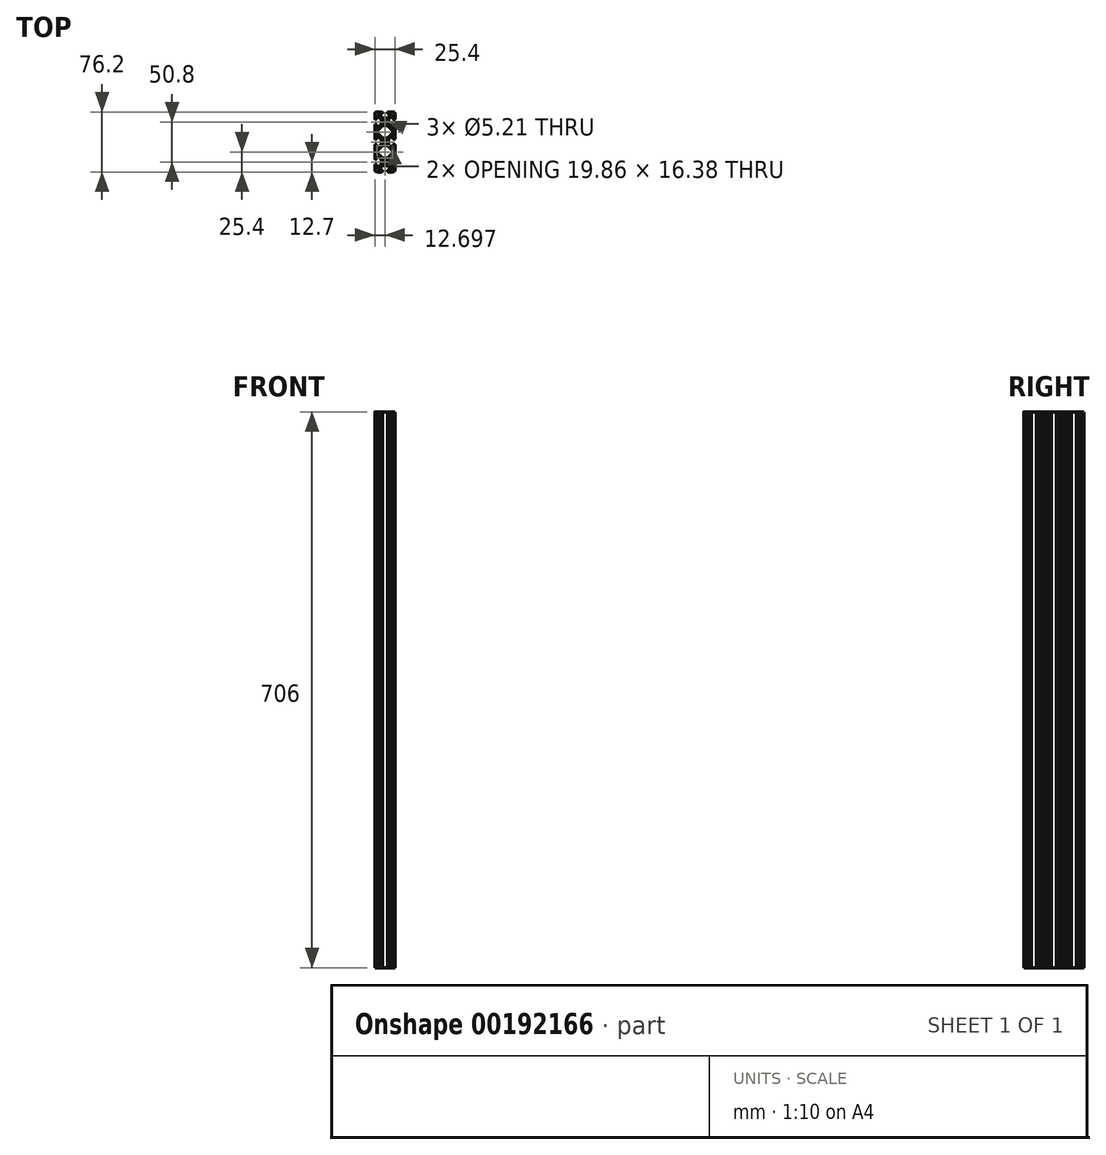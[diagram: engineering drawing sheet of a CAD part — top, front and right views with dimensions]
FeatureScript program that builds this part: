
annotation { "Feature Type Name" : "Feature", "Feature Type Description" : "" }
export const myFeature = defineFeature(function(context is Context, id is Id, definition is map)
    precondition{}
    {
        {
            var Q0;
            Q0=qCreatedBy(makeId("Top.planeOp"),FACE);
            var sketch = newSketch(context, id + "F0", { "sketchPlane" : qUnion([Q0])});
            skArc(sketch, "E0.0.0", {"start": v(-125.85, 41.51) * mm, "mid": v(-126.36, 41) * mm, "end": v(-126.87, 41.51) * mm});
            skArc(sketch, "E0.0.1", {"start": v(-126.87, 41.51) * mm, "mid": v(-128.39, 40.9) * mm, "end": v(-129, 39.38) * mm});
            skArc(sketch, "E0.0.2", {"start": v(-129, 39.38) * mm, "mid": v(-128.5, 38.87) * mm, "end": v(-129, 38.36) * mm});
            skLineSegment(sketch, "E0.0.3", {"start": v(-129, 38.36) * mm, "end": v(-129, 35.13) * mm});
            skArc(sketch, "E0.0.4", {"start": v(-129, 35.13) * mm, "mid": v(-128.5, 34.63) * mm, "end": v(-129, 34.12) * mm});
            skLineSegment(sketch, "E0.0.5", {"start": v(-129, 34.12) * mm, "end": v(-129, 33.11) * mm});
            skArc(sketch, "E0.0.6", {"start": v(-129, 33.11) * mm, "mid": v(-127.9, 32) * mm, "end": v(-126.8, 33.11) * mm});
            skLineSegment(sketch, "E0.0.7", {"start": v(-126.8, 33.11) * mm, "end": v(-126.8, 35.28) * mm});
            skArc(sketch, "E0.0.8", {"start": v(-126.8, 35.28) * mm, "mid": v(-126.17, 36.22) * mm, "end": v(-125.06, 36) * mm});
            skLineSegment(sketch, "E0.0.9", {"start": v(-125.06, 36) * mm, "end": v(-121.74, 32.69) * mm});
            skArc(sketch, "E0.0.10", {"start": v(-121.74, 32.69) * mm, "mid": v(-121.05, 31.66) * mm, "end": v(-120.81, 30.44) * mm});
            skLineSegment(sketch, "E0.0.11", {"start": v(-120.81, 30.44) * mm, "end": v(-120.81, 27.18) * mm});
            skArc(sketch, "E0.0.12", {"start": v(-120.81, 27.18) * mm, "mid": v(-121.05, 25.96) * mm, "end": v(-121.74, 24.93) * mm});
            skLineSegment(sketch, "E0.0.13", {"start": v(-121.74, 24.93) * mm, "end": v(-125.06, 21.62) * mm});
            skArc(sketch, "E0.0.14", {"start": v(-125.06, 21.62) * mm, "mid": v(-126.17, 21.4) * mm, "end": v(-126.8, 22.34) * mm});
            skLineSegment(sketch, "E0.0.15", {"start": v(-126.8, 22.34) * mm, "end": v(-126.8, 24.5) * mm});
            skArc(sketch, "E0.0.16", {"start": v(-126.8, 24.5) * mm, "mid": v(-127.9, 25.61) * mm, "end": v(-129, 24.5) * mm});
            skLineSegment(sketch, "E0.0.17", {"start": v(-129, 24.5) * mm, "end": v(-129, 23.5) * mm});
            skArc(sketch, "E0.0.18", {"start": v(-129, 23.5) * mm, "mid": v(-128.5, 23) * mm, "end": v(-129, 22.49) * mm});
            skLineSegment(sketch, "E0.0.19", {"start": v(-129, 22.49) * mm, "end": v(-129, 19.26) * mm});
            skArc(sketch, "E0.0.20", {"start": v(-129, 19.26) * mm, "mid": v(-128.5, 18.75) * mm, "end": v(-129, 18.24) * mm});
            skLineSegment(sketch, "E0.0.21", {"start": v(-129, 18.24) * mm, "end": v(-129, 13.98) * mm});
            skArc(sketch, "E0.0.22", {"start": v(-129, 13.98) * mm, "mid": v(-128.5, 13.47) * mm, "end": v(-129, 12.96) * mm});
            skLineSegment(sketch, "E0.0.23", {"start": v(-129, 12.96) * mm, "end": v(-129, 9.73) * mm});
            skArc(sketch, "E0.0.24", {"start": v(-129, 9.73) * mm, "mid": v(-128.5, 9.23) * mm, "end": v(-129, 8.72) * mm});
            skLineSegment(sketch, "E0.0.25", {"start": v(-129, 8.72) * mm, "end": v(-129, 7.71) * mm});
            skArc(sketch, "E0.0.26", {"start": v(-129, 7.71) * mm, "mid": v(-127.9, 6.6) * mm, "end": v(-126.8, 7.71) * mm});
            skLineSegment(sketch, "E0.0.27", {"start": v(-126.8, 7.71) * mm, "end": v(-126.8, 9.88) * mm});
            skArc(sketch, "E0.0.28", {"start": v(-126.8, 9.88) * mm, "mid": v(-126.17, 10.82) * mm, "end": v(-125.06, 10.6) * mm});
            skLineSegment(sketch, "E0.0.29", {"start": v(-125.06, 10.6) * mm, "end": v(-121.74, 7.29) * mm});
            skArc(sketch, "E0.0.30", {"start": v(-121.74, 7.29) * mm, "mid": v(-121.05, 6.26) * mm, "end": v(-120.81, 5.04) * mm});
            skLineSegment(sketch, "E0.0.31", {"start": v(-120.81, 5.04) * mm, "end": v(-120.81, 1.78) * mm});
            skArc(sketch, "E0.0.32", {"start": v(-120.81, 1.78) * mm, "mid": v(-121.05, 0.56) * mm, "end": v(-121.74, -0.47) * mm});
            skLineSegment(sketch, "E0.0.33", {"start": v(-121.74, -0.47) * mm, "end": v(-125.06, -3.78) * mm});
            skArc(sketch, "E0.0.34", {"start": v(-125.06, -3.78) * mm, "mid": v(-126.17, -4) * mm, "end": v(-126.8, -3.06) * mm});
            skLineSegment(sketch, "E0.0.35", {"start": v(-126.8, -3.06) * mm, "end": v(-126.8, -0.9) * mm});
            skArc(sketch, "E0.0.36", {"start": v(-126.8, -0.9) * mm, "mid": v(-127.9, 0.21) * mm, "end": v(-129, -0.9) * mm});
            skLineSegment(sketch, "E0.0.37", {"start": v(-129, -0.9) * mm, "end": v(-129, -1.9) * mm});
            skArc(sketch, "E0.0.38", {"start": v(-129, -1.9) * mm, "mid": v(-128.5, -2.4) * mm, "end": v(-129, -2.91) * mm});
            skLineSegment(sketch, "E0.0.39", {"start": v(-129, -2.91) * mm, "end": v(-129, -6.14) * mm});
            skArc(sketch, "E0.0.40", {"start": v(-129, -6.14) * mm, "mid": v(-128.5, -6.65) * mm, "end": v(-129, -7.16) * mm});
            skLineSegment(sketch, "E0.0.41", {"start": v(-129, -7.16) * mm, "end": v(-129, -11.42) * mm});
            skArc(sketch, "E0.0.42", {"start": v(-129, -11.42) * mm, "mid": v(-128.5, -11.93) * mm, "end": v(-129, -12.44) * mm});
            skLineSegment(sketch, "E0.0.43", {"start": v(-129, -12.44) * mm, "end": v(-129, -15.67) * mm});
            skArc(sketch, "E0.0.44", {"start": v(-129, -15.67) * mm, "mid": v(-128.5, -16.17) * mm, "end": v(-129, -16.68) * mm});
            skLineSegment(sketch, "E0.0.45", {"start": v(-129, -16.68) * mm, "end": v(-129, -17.69) * mm});
            skArc(sketch, "E0.0.46", {"start": v(-129, -17.69) * mm, "mid": v(-127.9, -18.8) * mm, "end": v(-126.8, -17.69) * mm});
            skLineSegment(sketch, "E0.0.47", {"start": v(-126.8, -17.69) * mm, "end": v(-126.8, -15.52) * mm});
            skArc(sketch, "E0.0.48", {"start": v(-126.8, -15.52) * mm, "mid": v(-126.17, -14.58) * mm, "end": v(-125.06, -14.8) * mm});
            skLineSegment(sketch, "E0.0.49", {"start": v(-125.06, -14.8) * mm, "end": v(-121.74, -18.11) * mm});
            skArc(sketch, "E0.0.50", {"start": v(-121.74, -18.11) * mm, "mid": v(-121.05, -19.14) * mm, "end": v(-120.81, -20.36) * mm});
            skLineSegment(sketch, "E0.0.51", {"start": v(-120.81, -20.36) * mm, "end": v(-120.81, -23.62) * mm});
            skArc(sketch, "E0.0.52", {"start": v(-120.81, -23.62) * mm, "mid": v(-121.05, -24.84) * mm, "end": v(-121.74, -25.87) * mm});
            skLineSegment(sketch, "E0.0.53", {"start": v(-121.74, -25.87) * mm, "end": v(-125.06, -29.18) * mm});
            skArc(sketch, "E0.0.54", {"start": v(-125.06, -29.18) * mm, "mid": v(-126.17, -29.4) * mm, "end": v(-126.8, -28.46) * mm});
            skLineSegment(sketch, "E0.0.55", {"start": v(-126.8, -28.46) * mm, "end": v(-126.8, -26.3) * mm});
            skArc(sketch, "E0.0.56", {"start": v(-126.8, -26.3) * mm, "mid": v(-127.9, -25.19) * mm, "end": v(-129, -26.3) * mm});
            skLineSegment(sketch, "E0.0.57", {"start": v(-129, -26.3) * mm, "end": v(-129, -27.3) * mm});
            skArc(sketch, "E0.0.58", {"start": v(-129, -27.3) * mm, "mid": v(-128.5, -27.8) * mm, "end": v(-129, -28.31) * mm});
            skLineSegment(sketch, "E0.0.59", {"start": v(-129, -28.31) * mm, "end": v(-129, -31.54) * mm});
            skArc(sketch, "E0.0.60", {"start": v(-129, -31.54) * mm, "mid": v(-128.5, -32.05) * mm, "end": v(-129, -32.56) * mm});
            skArc(sketch, "E0.0.61", {"start": v(-129, -32.56) * mm, "mid": v(-128.39, -34.07) * mm, "end": v(-126.87, -34.69) * mm});
            skArc(sketch, "E0.0.62", {"start": v(-126.87, -34.69) * mm, "mid": v(-126.36, -34.18) * mm, "end": v(-125.85, -34.69) * mm});
            skLineSegment(sketch, "E0.0.63", {"start": v(-125.85, -34.69) * mm, "end": v(-122.63, -34.69) * mm});
            skArc(sketch, "E0.0.64", {"start": v(-122.63, -34.69) * mm, "mid": v(-122.12, -34.18) * mm, "end": v(-121.61, -34.69) * mm});
            skLineSegment(sketch, "E0.0.65", {"start": v(-121.61, -34.69) * mm, "end": v(-120.6, -34.69) * mm});
            skArc(sketch, "E0.0.66", {"start": v(-120.6, -34.69) * mm, "mid": v(-119.5, -33.59) * mm, "end": v(-120.6, -32.48) * mm});
            skLineSegment(sketch, "E0.0.67", {"start": v(-120.6, -32.48) * mm, "end": v(-122.78, -32.48) * mm});
            skArc(sketch, "E0.0.68", {"start": v(-122.78, -32.48) * mm, "mid": v(-123.72, -31.85) * mm, "end": v(-123.5, -30.75) * mm});
            skLineSegment(sketch, "E0.0.69", {"start": v(-123.5, -30.75) * mm, "end": v(-120.18, -27.43) * mm});
            skArc(sketch, "E0.0.70", {"start": v(-120.18, -27.43) * mm, "mid": v(-119.15, -26.74) * mm, "end": v(-117.93, -26.5) * mm});
            skLineSegment(sketch, "E0.0.71", {"start": v(-117.93, -26.5) * mm, "end": v(-114.67, -26.5) * mm});
            skArc(sketch, "E0.0.72", {"start": v(-114.67, -26.5) * mm, "mid": v(-113.46, -26.74) * mm, "end": v(-112.43, -27.43) * mm});
            skLineSegment(sketch, "E0.0.73", {"start": v(-112.43, -27.43) * mm, "end": v(-109.11, -30.75) * mm});
            skArc(sketch, "E0.0.74", {"start": v(-109.11, -30.75) * mm, "mid": v(-108.89, -31.85) * mm, "end": v(-109.83, -32.48) * mm});
            skLineSegment(sketch, "E0.0.75", {"start": v(-109.83, -32.48) * mm, "end": v(-112, -32.48) * mm});
            skArc(sketch, "E0.0.76", {"start": v(-112, -32.48) * mm, "mid": v(-113.1, -33.59) * mm, "end": v(-112, -34.69) * mm});
            skLineSegment(sketch, "E0.0.77", {"start": v(-112, -34.69) * mm, "end": v(-111, -34.69) * mm});
            skArc(sketch, "E0.0.78", {"start": v(-111, -34.69) * mm, "mid": v(-110.49, -34.18) * mm, "end": v(-109.98, -34.69) * mm});
            skLineSegment(sketch, "E0.0.79", {"start": v(-109.98, -34.69) * mm, "end": v(-106.75, -34.69) * mm});
            skArc(sketch, "E0.0.80", {"start": v(-106.75, -34.69) * mm, "mid": v(-106.24, -34.18) * mm, "end": v(-105.74, -34.69) * mm});
            skArc(sketch, "E0.0.81", {"start": v(-105.74, -34.69) * mm, "mid": v(-104.22, -34.07) * mm, "end": v(-103.6, -32.56) * mm});
            skArc(sketch, "E0.0.82", {"start": v(-103.6, -32.56) * mm, "mid": v(-104.11, -32.05) * mm, "end": v(-103.6, -31.54) * mm});
            skLineSegment(sketch, "E0.0.83", {"start": v(-103.6, -31.54) * mm, "end": v(-103.6, -28.31) * mm});
            skArc(sketch, "E0.0.84", {"start": v(-103.6, -28.31) * mm, "mid": v(-104.11, -27.8) * mm, "end": v(-103.6, -27.3) * mm});
            skLineSegment(sketch, "E0.0.85", {"start": v(-103.6, -27.3) * mm, "end": v(-103.6, -26.3) * mm});
            skArc(sketch, "E0.0.86", {"start": v(-103.6, -26.3) * mm, "mid": v(-104.7, -25.19) * mm, "end": v(-105.81, -26.3) * mm});
            skLineSegment(sketch, "E0.0.87", {"start": v(-105.81, -26.3) * mm, "end": v(-105.81, -28.46) * mm});
            skArc(sketch, "E0.0.88", {"start": v(-105.81, -28.46) * mm, "mid": v(-106.44, -29.4) * mm, "end": v(-107.55, -29.18) * mm});
            skLineSegment(sketch, "E0.0.89", {"start": v(-107.55, -29.18) * mm, "end": v(-110.86, -25.87) * mm});
            skArc(sketch, "E0.0.90", {"start": v(-110.86, -25.87) * mm, "mid": v(-111.55, -24.84) * mm, "end": v(-111.8, -23.62) * mm});
            skLineSegment(sketch, "E0.0.91", {"start": v(-111.8, -23.62) * mm, "end": v(-111.8, -20.36) * mm});
            skArc(sketch, "E0.0.92", {"start": v(-111.8, -20.36) * mm, "mid": v(-111.55, -19.14) * mm, "end": v(-110.86, -18.11) * mm});
            skLineSegment(sketch, "E0.0.93", {"start": v(-110.86, -18.11) * mm, "end": v(-107.55, -14.8) * mm});
            skArc(sketch, "E0.0.94", {"start": v(-107.55, -14.8) * mm, "mid": v(-106.44, -14.58) * mm, "end": v(-105.81, -15.52) * mm});
            skLineSegment(sketch, "E0.0.95", {"start": v(-105.81, -15.52) * mm, "end": v(-105.81, -17.69) * mm});
            skArc(sketch, "E0.0.96", {"start": v(-105.81, -17.69) * mm, "mid": v(-104.7, -18.8) * mm, "end": v(-103.6, -17.69) * mm});
            skLineSegment(sketch, "E0.0.97", {"start": v(-103.6, -17.69) * mm, "end": v(-103.6, -16.68) * mm});
            skArc(sketch, "E0.0.98", {"start": v(-103.6, -16.68) * mm, "mid": v(-104.11, -16.17) * mm, "end": v(-103.6, -15.67) * mm});
            skLineSegment(sketch, "E0.0.99", {"start": v(-103.6, -15.67) * mm, "end": v(-103.6, -12.44) * mm});
            skArc(sketch, "E0.0.100", {"start": v(-103.6, -12.44) * mm, "mid": v(-104.11, -11.93) * mm, "end": v(-103.6, -11.42) * mm});
            skLineSegment(sketch, "E0.0.101", {"start": v(-103.6, -11.42) * mm, "end": v(-103.6, -7.16) * mm});
            skArc(sketch, "E0.0.102", {"start": v(-103.6, -7.16) * mm, "mid": v(-104.11, -6.65) * mm, "end": v(-103.6, -6.14) * mm});
            skLineSegment(sketch, "E0.0.103", {"start": v(-103.6, -6.14) * mm, "end": v(-103.6, -2.91) * mm});
            skArc(sketch, "E0.0.104", {"start": v(-103.6, -2.91) * mm, "mid": v(-104.11, -2.4) * mm, "end": v(-103.6, -1.9) * mm});
            skLineSegment(sketch, "E0.0.105", {"start": v(-103.6, -1.9) * mm, "end": v(-103.6, -0.9) * mm});
            skArc(sketch, "E0.0.106", {"start": v(-103.6, -0.9) * mm, "mid": v(-104.7, 0.21) * mm, "end": v(-105.81, -0.9) * mm});
            skLineSegment(sketch, "E0.0.107", {"start": v(-105.81, -0.9) * mm, "end": v(-105.81, -3.06) * mm});
            skArc(sketch, "E0.0.108", {"start": v(-105.81, -3.06) * mm, "mid": v(-106.44, -4) * mm, "end": v(-107.55, -3.78) * mm});
            skLineSegment(sketch, "E0.0.109", {"start": v(-107.55, -3.78) * mm, "end": v(-110.86, -0.47) * mm});
            skArc(sketch, "E0.0.110", {"start": v(-110.86, -0.47) * mm, "mid": v(-111.55, 0.56) * mm, "end": v(-111.8, 1.78) * mm});
            skLineSegment(sketch, "E0.0.111", {"start": v(-111.8, 1.78) * mm, "end": v(-111.8, 5.04) * mm});
            skArc(sketch, "E0.0.112", {"start": v(-111.8, 5.04) * mm, "mid": v(-111.55, 6.26) * mm, "end": v(-110.86, 7.29) * mm});
            skLineSegment(sketch, "E0.0.113", {"start": v(-110.86, 7.29) * mm, "end": v(-107.55, 10.6) * mm});
            skArc(sketch, "E0.0.114", {"start": v(-107.55, 10.6) * mm, "mid": v(-106.44, 10.82) * mm, "end": v(-105.81, 9.88) * mm});
            skLineSegment(sketch, "E0.0.115", {"start": v(-105.81, 9.88) * mm, "end": v(-105.81, 7.71) * mm});
            skArc(sketch, "E0.0.116", {"start": v(-105.81, 7.71) * mm, "mid": v(-104.7, 6.6) * mm, "end": v(-103.6, 7.71) * mm});
            skLineSegment(sketch, "E0.0.117", {"start": v(-103.6, 7.71) * mm, "end": v(-103.6, 8.72) * mm});
            skArc(sketch, "E0.0.118", {"start": v(-103.6, 8.72) * mm, "mid": v(-104.11, 9.23) * mm, "end": v(-103.6, 9.73) * mm});
            skLineSegment(sketch, "E0.0.119", {"start": v(-103.6, 9.73) * mm, "end": v(-103.6, 12.96) * mm});
            skArc(sketch, "E0.0.120", {"start": v(-103.6, 12.96) * mm, "mid": v(-104.11, 13.47) * mm, "end": v(-103.6, 13.98) * mm});
            skLineSegment(sketch, "E0.0.121", {"start": v(-103.6, 13.98) * mm, "end": v(-103.6, 18.24) * mm});
            skArc(sketch, "E0.0.122", {"start": v(-103.6, 18.24) * mm, "mid": v(-104.11, 18.75) * mm, "end": v(-103.6, 19.26) * mm});
            skLineSegment(sketch, "E0.0.123", {"start": v(-103.6, 19.26) * mm, "end": v(-103.6, 22.49) * mm});
            skArc(sketch, "E0.0.124", {"start": v(-103.6, 22.49) * mm, "mid": v(-104.11, 23) * mm, "end": v(-103.6, 23.5) * mm});
            skLineSegment(sketch, "E0.0.125", {"start": v(-103.6, 23.5) * mm, "end": v(-103.6, 24.5) * mm});
            skArc(sketch, "E0.0.126", {"start": v(-103.6, 24.5) * mm, "mid": v(-104.7, 25.61) * mm, "end": v(-105.81, 24.5) * mm});
            skLineSegment(sketch, "E0.0.127", {"start": v(-105.81, 24.5) * mm, "end": v(-105.81, 22.34) * mm});
            skArc(sketch, "E0.0.128", {"start": v(-105.81, 22.34) * mm, "mid": v(-106.44, 21.4) * mm, "end": v(-107.55, 21.62) * mm});
            skLineSegment(sketch, "E0.0.129", {"start": v(-107.55, 21.62) * mm, "end": v(-110.86, 24.93) * mm});
            skArc(sketch, "E0.0.130", {"start": v(-110.86, 24.93) * mm, "mid": v(-111.55, 25.96) * mm, "end": v(-111.8, 27.18) * mm});
            skLineSegment(sketch, "E0.0.131", {"start": v(-111.8, 27.18) * mm, "end": v(-111.8, 30.44) * mm});
            skArc(sketch, "E0.0.132", {"start": v(-111.8, 30.44) * mm, "mid": v(-111.55, 31.66) * mm, "end": v(-110.86, 32.69) * mm});
            skLineSegment(sketch, "E0.0.133", {"start": v(-110.86, 32.69) * mm, "end": v(-107.55, 36) * mm});
            skArc(sketch, "E0.0.134", {"start": v(-107.55, 36) * mm, "mid": v(-106.44, 36.22) * mm, "end": v(-105.81, 35.28) * mm});
            skLineSegment(sketch, "E0.0.135", {"start": v(-105.81, 35.28) * mm, "end": v(-105.81, 33.11) * mm});
            skArc(sketch, "E0.0.136", {"start": v(-105.81, 33.11) * mm, "mid": v(-104.7, 32) * mm, "end": v(-103.6, 33.11) * mm});
            skLineSegment(sketch, "E0.0.137", {"start": v(-103.6, 33.11) * mm, "end": v(-103.6, 34.12) * mm});
            skArc(sketch, "E0.0.138", {"start": v(-103.6, 34.12) * mm, "mid": v(-104.11, 34.63) * mm, "end": v(-103.6, 35.13) * mm});
            skLineSegment(sketch, "E0.0.139", {"start": v(-103.6, 35.13) * mm, "end": v(-103.6, 38.36) * mm});
            skArc(sketch, "E0.0.140", {"start": v(-103.6, 38.36) * mm, "mid": v(-104.11, 38.87) * mm, "end": v(-103.6, 39.38) * mm});
            skArc(sketch, "E0.0.141", {"start": v(-103.6, 39.38) * mm, "mid": v(-104.22, 40.9) * mm, "end": v(-105.74, 41.51) * mm});
            skArc(sketch, "E0.0.142", {"start": v(-105.74, 41.51) * mm, "mid": v(-106.24, 41) * mm, "end": v(-106.75, 41.51) * mm});
            skLineSegment(sketch, "E0.0.143", {"start": v(-106.75, 41.51) * mm, "end": v(-109.98, 41.51) * mm});
            skArc(sketch, "E0.0.144", {"start": v(-109.98, 41.51) * mm, "mid": v(-110.49, 41) * mm, "end": v(-111, 41.51) * mm});
            skLineSegment(sketch, "E0.0.145", {"start": v(-111, 41.51) * mm, "end": v(-112, 41.51) * mm});
            skArc(sketch, "E0.0.146", {"start": v(-112, 41.51) * mm, "mid": v(-113.1, 40.4) * mm, "end": v(-112, 39.3) * mm});
            skLineSegment(sketch, "E0.0.147", {"start": v(-112, 39.3) * mm, "end": v(-109.83, 39.3) * mm});
            skArc(sketch, "E0.0.148", {"start": v(-109.83, 39.3) * mm, "mid": v(-108.89, 38.67) * mm, "end": v(-109.11, 37.57) * mm});
            skLineSegment(sketch, "E0.0.149", {"start": v(-109.11, 37.57) * mm, "end": v(-112.43, 34.25) * mm});
            skArc(sketch, "E0.0.150", {"start": v(-112.43, 34.25) * mm, "mid": v(-113.46, 33.56) * mm, "end": v(-114.67, 33.32) * mm});
            skLineSegment(sketch, "E0.0.151", {"start": v(-114.67, 33.32) * mm, "end": v(-117.93, 33.32) * mm});
            skArc(sketch, "E0.0.152", {"start": v(-117.93, 33.32) * mm, "mid": v(-119.15, 33.56) * mm, "end": v(-120.18, 34.25) * mm});
            skLineSegment(sketch, "E0.0.153", {"start": v(-120.18, 34.25) * mm, "end": v(-123.5, 37.57) * mm});
            skArc(sketch, "E0.0.154", {"start": v(-123.5, 37.57) * mm, "mid": v(-123.72, 38.67) * mm, "end": v(-122.78, 39.3) * mm});
            skLineSegment(sketch, "E0.0.155", {"start": v(-122.78, 39.3) * mm, "end": v(-120.6, 39.3) * mm});
            skArc(sketch, "E0.0.156", {"start": v(-120.6, 39.3) * mm, "mid": v(-119.5, 40.4) * mm, "end": v(-120.6, 41.51) * mm});
            skLineSegment(sketch, "E0.0.157", {"start": v(-120.6, 41.51) * mm, "end": v(-121.61, 41.51) * mm});
            skArc(sketch, "E0.0.158", {"start": v(-121.61, 41.51) * mm, "mid": v(-122.12, 41) * mm, "end": v(-122.63, 41.51) * mm});
            skLineSegment(sketch, "E0.0.159", {"start": v(-122.63, 41.51) * mm, "end": v(-125.85, 41.51) * mm});
            skCircle(sketch, "E1.0", {"center": v(-116.3, 3.41) * mm, "radius": 2.6 * mm});
            skCircle(sketch, "E2.0", {"center": v(-116.3, -21.99) * mm, "radius": 2.6 * mm});
            skCircle(sketch, "E3.0", {"center": v(-116.3, 28.81) * mm, "radius": 2.6 * mm});
            skArc(sketch, "E4.0", {"start": v(-120.18, 8.85) * mm, "mid": v(-119.15, 8.16) * mm, "end": v(-117.93, 7.92) * mm});
            skArc(sketch, "E4.1", {"start": v(-117.93, 24.3) * mm, "mid": v(-119.15, 24.06) * mm, "end": v(-120.18, 23.37) * mm});
            skLineSegment(sketch, "E4.2", {"start": v(-117.93, -17.48) * mm, "end": v(-114.67, -17.48) * mm});
            skLineSegment(sketch, "E4.3", {"start": v(-114.67, 24.3) * mm, "end": v(-117.93, 24.3) * mm});
            skArc(sketch, "E4.4", {"start": v(-114.67, 7.92) * mm, "mid": v(-113.46, 8.16) * mm, "end": v(-112.43, 8.85) * mm});
            skArc(sketch, "E4.5", {"start": v(-117.93, -1.1) * mm, "mid": v(-119.15, -1.34) * mm, "end": v(-120.18, -2.03) * mm});
            skArc(sketch, "E4.6", {"start": v(-112.43, -2.03) * mm, "mid": v(-113.46, -1.34) * mm, "end": v(-114.67, -1.1) * mm});
            skArc(sketch, "E4.7", {"start": v(-120.18, -16.55) * mm, "mid": v(-119.15, -17.24) * mm, "end": v(-117.93, -17.48) * mm});
            skLineSegment(sketch, "E4.8", {"start": v(-114.67, -1.1) * mm, "end": v(-117.93, -1.1) * mm});
            skLineSegment(sketch, "E4.9", {"start": v(-117.93, 7.92) * mm, "end": v(-114.67, 7.92) * mm});
            skArc(sketch, "E4.21", {"start": v(-114.67, -17.48) * mm, "mid": v(-113.46, -17.24) * mm, "end": v(-112.43, -16.55) * mm});
            skArc(sketch, "E4.23", {"start": v(-112.43, 23.37) * mm, "mid": v(-113.46, 24.06) * mm, "end": v(-114.67, 24.3) * mm});
            skLineSegment(sketch, "E4.25", {"start": v(-106.83, -7.62) * mm, "end": v(-112.43, -2.03) * mm});
            skLineSegment(sketch, "E4.26", {"start": v(-125.77, -10.96) * mm, "end": v(-120.18, -16.55) * mm});
            skLineSegment(sketch, "E4.27", {"start": v(-120.18, -2.03) * mm, "end": v(-125.77, -7.62) * mm});
            skLineSegment(sketch, "E4.28", {"start": v(-125.77, 14.44) * mm, "end": v(-120.18, 8.85) * mm});
            skLineSegment(sketch, "E4.29", {"start": v(-120.18, 23.37) * mm, "end": v(-125.77, 17.78) * mm});
            skLineSegment(sketch, "E4.31", {"start": v(-106.83, 17.78) * mm, "end": v(-112.43, 23.37) * mm});
            skLineSegment(sketch, "E4.32", {"start": v(-112.43, 8.85) * mm, "end": v(-106.83, 14.44) * mm});
            skLineSegment(sketch, "E4.56", {"start": v(-112.43, -16.55) * mm, "end": v(-106.83, -10.96) * mm});
            skArc(sketch, "E4.92", {"start": v(-126.23, 15.56) * mm, "mid": v(-126.11, 14.95) * mm, "end": v(-125.77, 14.44) * mm});
            skArc(sketch, "E4.95", {"start": v(-125.77, 17.78) * mm, "mid": v(-126.11, 17.27) * mm, "end": v(-126.23, 16.66) * mm});
            skArc(sketch, "E4.99", {"start": v(-126.23, -9.84) * mm, "mid": v(-126.11, -10.45) * mm, "end": v(-125.77, -10.96) * mm});
            skArc(sketch, "E4.100", {"start": v(-106.83, -10.96) * mm, "mid": v(-106.5, -10.45) * mm, "end": v(-106.37, -9.84) * mm});
            skLineSegment(sketch, "E4.105", {"start": v(-126.23, -8.74) * mm, "end": v(-126.23, -9.84) * mm});
            skArc(sketch, "E4.116", {"start": v(-106.83, 14.44) * mm, "mid": v(-106.5, 14.95) * mm, "end": v(-106.37, 15.56) * mm});
            skLineSegment(sketch, "E4.117", {"start": v(-126.23, 16.66) * mm, "end": v(-126.23, 15.56) * mm});
            skArc(sketch, "E4.120", {"start": v(-106.37, 16.66) * mm, "mid": v(-106.5, 17.27) * mm, "end": v(-106.83, 17.78) * mm});
            skArc(sketch, "E4.127", {"start": v(-125.77, -7.62) * mm, "mid": v(-126.11, -8.13) * mm, "end": v(-126.23, -8.74) * mm});
            skLineSegment(sketch, "E4.128", {"start": v(-106.37, -9.84) * mm, "end": v(-106.37, -8.74) * mm});
            skLineSegment(sketch, "E4.140", {"start": v(-106.37, 15.56) * mm, "end": v(-106.37, 16.66) * mm});
            skArc(sketch, "E4.141", {"start": v(-106.37, -8.74) * mm, "mid": v(-106.5, -8.13) * mm, "end": v(-106.83, -7.62) * mm});
            skSolve(sketch);
        }
        {
            var Q0;
            Q0=makeQuery(id+"F0.imprint","IMPRINT",FACE,{"disambiguationData":[TD([[makeQuery(id+"F0.imprint","IMPRINT",EDGE,{"derivedFrom":sQuery(id+"F0.wireOp",EDGE,"E4.0")}),-1.0]])]});
            extrude(context, id + "F1", {"entities" : qUnion([Q0]), "depth" : 706 * mm});
        }
    });
